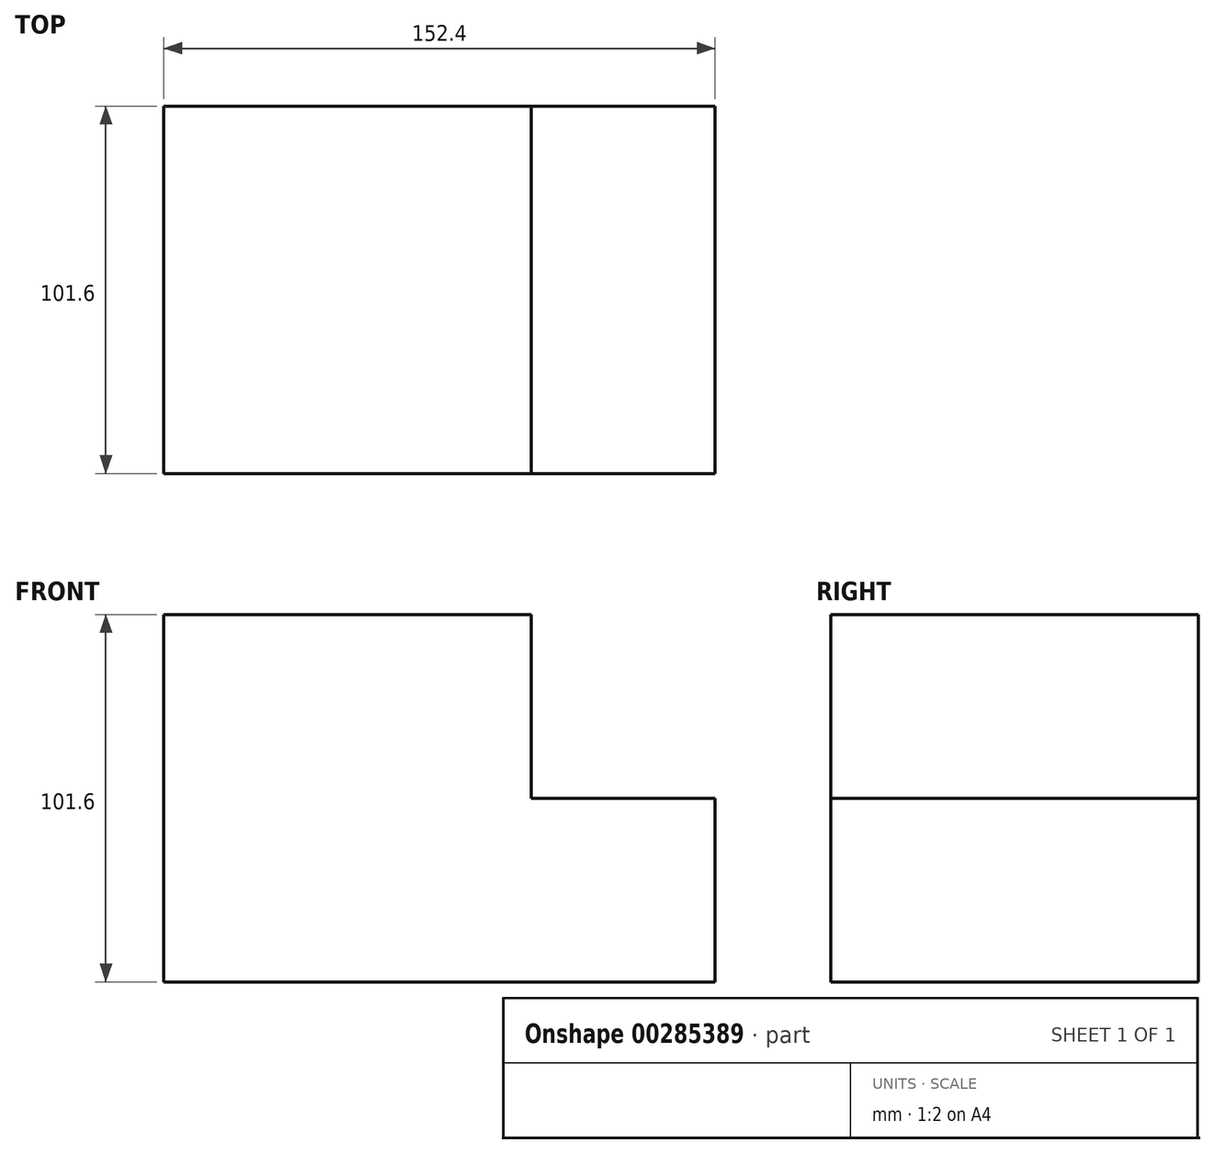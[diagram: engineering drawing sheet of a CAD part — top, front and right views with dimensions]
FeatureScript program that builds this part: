
annotation { "Feature Type Name" : "Feature", "Feature Type Description" : "" }
export const myFeature = defineFeature(function(context is Context, id is Id, definition is map)
    precondition{}
    {
        {
            var Q0;
            Q0=qCreatedBy(makeId("Front.planeOp"),FACE);
            var sketch = newSketch(context, id + "F0", { "sketchPlane" : qUnion([Q0])});
            skLineSegment(sketch, "E0", {"start": v(-101.6, 0) * mm, "end": v(50.8, 0) * mm});
            skLineSegment(sketch, "E1", {"start": v(50.8, 0) * mm, "end": v(50.8, 50.8) * mm});
            skLineSegment(sketch, "E2", {"start": v(50.8, 50.8) * mm, "end": v(0, 50.8) * mm});
            skLineSegment(sketch, "E3", {"start": v(0, 50.8) * mm, "end": v(0, 101.6) * mm});
            skLineSegment(sketch, "E4", {"start": v(0, 101.6) * mm, "end": v(-101.6, 101.6) * mm});
            skLineSegment(sketch, "E5", {"start": v(-101.6, 101.6) * mm, "end": v(-101.6, 0) * mm});
            skSolve(sketch);
        }
        {
            var Q0;
            Q0 = qSketchRegion(id + "F0", true);
            extrude(context, id + "F1", {"entities" : qUnion([Q0]), "depth" : 101.6 * mm});
        }
    });
